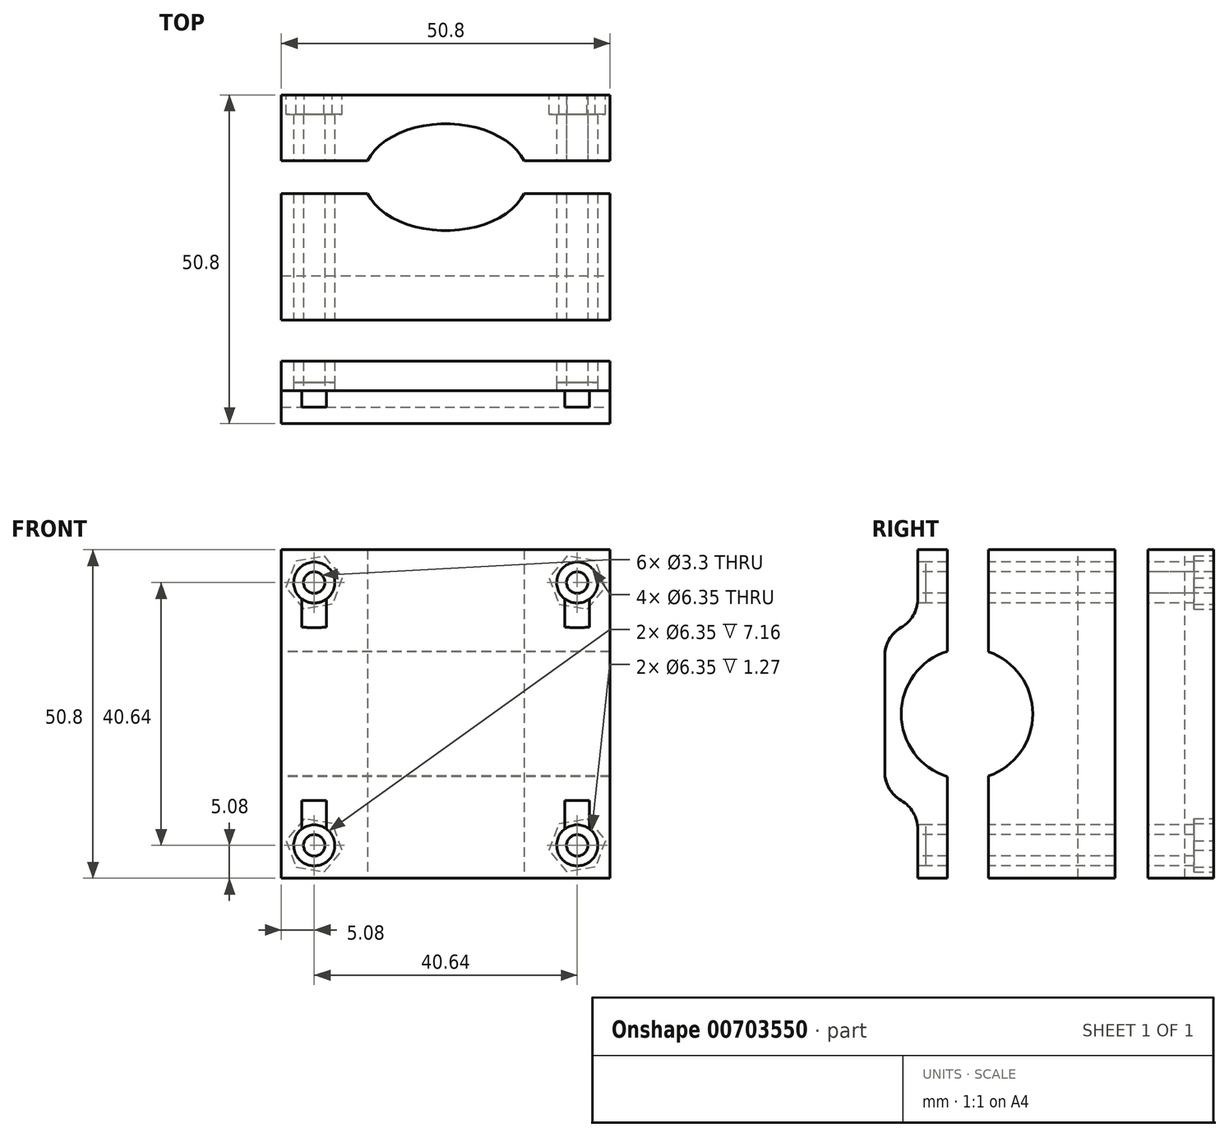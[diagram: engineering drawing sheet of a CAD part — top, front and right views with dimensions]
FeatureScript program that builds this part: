
annotation { "Feature Type Name" : "Feature", "Feature Type Description" : "" }
export const myFeature = defineFeature(function(context is Context, id is Id, definition is map)
    precondition{}
    {
        {
            var Q0;
            Q0=qCreatedBy(makeId("Top.planeOp"),FACE);
            var sketch = newSketch(context, id + "F0", { "sketchPlane" : qUnion([Q0])});
            skLineSegment(sketch, "E0.bottom", {"start": v(-25.4, -12.7) * mm, "end": v(25.4, -12.7) * mm});
            skLineSegment(sketch, "E0.top", {"start": v(-25.4, 12.7) * mm, "end": v(25.4, 12.7) * mm});
            skLineSegment(sketch, "E0.left", {"start": v(-25.4, -12.7) * mm, "end": v(-25.4, 12.7) * mm});
            skLineSegment(sketch, "E0.right", {"start": v(25.4, -12.7) * mm, "end": v(25.4, 12.7) * mm});
            skLineSegment(sketch, "E1.bottom", {"start": v(-25.4, 2.54) * mm, "end": v(25.4, 2.54) * mm});
            skLineSegment(sketch, "E1.top", {"start": v(-25.4, -2.54) * mm, "end": v(25.4, -2.54) * mm});
            skLineSegment(sketch, "E1.left", {"start": v(-25.4, 2.54) * mm, "end": v(-25.4, -2.54) * mm});
            skLineSegment(sketch, "E1.right", {"start": v(25.4, 2.54) * mm, "end": v(25.4, -2.54) * mm});
            skEllipse(sketch, "E2", {"center": v(0, 0) * mm, "majorRadius": 12.7 * mm, "minorRadius": 8.26 * mm, "majorAxis": v(1, 0)});
            skSolve(sketch);
        }
        {
            var Q0;
            {var subQ6=sQuery(id+"F0.wireOp",EDGE,"E0.top");Q0=makeQuery(id+"F0.imprint","IMPRINT",FACE,{"disambiguationData":[TD([[makeQuery(id+"F0.imprint","IMPRINT",EDGE,{"derivedFrom":subQ6}),-1.0]])]});}
            var Q1;
            {var subQ5=sQuery(id+"F0.wireOp",EDGE,"E0.bottom");Q1=makeQuery(id+"F0.imprint","IMPRINT",FACE,{"disambiguationData":[TD([[makeQuery(id+"F0.imprint","IMPRINT",EDGE,{"derivedFrom":subQ5}),1.0]])]});}
            extrude(context, id + "F1", {"entities" : qUnion([Q0, Q1]), "depth" : 25.4 * mm, "offsetDistance" : 25.4 * mm});
        }
        {
            var Q0;
            Q0=makeQuery(id+"F1.opExtrude","SWEPT_FACE",FACE,{"disambiguationData":[OSD([sQuery(id+"F0.wireOp",EDGE,"E0.bottom")])]});
            extrude(context, id + "F2", {"entities" : qUnion([Q0]), "operationType" : NewBodyOperationType.ADD, "depth" : 25.4 * mm, "offsetDistance" : 25.4 * mm});
        }
        {
            var Q0;
            {var subQ0=sQuery(id+"F0.wireOp",EDGE,"E0.right");var subQ1=sQuery(id+"F0.wireOp",EDGE,"E0.bottom");Q0=makeQuery(id+"F2.boolean.opBoolean","MERGE",FACE,{"derivedFrom":[makeQuery(id+"F1.opExtrude","SWEPT_FACE",FACE,{"disambiguationData":[OSD([subQ0]),TDD([makeQuery(id+"F0.imprint","IMPRINT",EDGE,{"disambiguationData":[TD([[makeQuery(id+"F0.imprint","INTERSECT",VERTEX,{"derivedFrom":[subQ1,subQ0]}),-1.0]])],"derivedFrom":subQ0})])]}),makeQuery(id+"F2.opExtrude","SWEPT_FACE",FACE,{"disambiguationData":[OSD([subQ1,subQ0])]})]});}
            var sketch = newSketch(context, id + "F3", { "sketchPlane" : qUnion([Q0])});
            skCircle(sketch, "E3", {"center": v(-25.4, 12.7) * mm, "radius": 10.16 * mm});
            skSolve(sketch);
        }
        {
            var Q0;
            Q0=makeQuery(id+"F3.imprint","IMPRINT",FACE,{"disambiguationData":[TD([[makeQuery(id+"F3.imprint","IMPRINT",EDGE,{"derivedFrom":sQuery(id+"F3.wireOp",EDGE,"E3")}),1.0]])]});
            extrude(context, id + "F4", {"entities" : qUnion([Q0]), "operationType" : NewBodyOperationType.REMOVE, "endBound" : BoundingType.THROUGH_ALL, "oppositeDirection" : true, "depth" : 25.4 * mm, "offsetDistance" : 25.4 * mm});
        }
        {
            var Q0;
            {var subQ0=sQuery(id+"F0.wireOp",EDGE,"E0.bottom");Q0=makeQuery(id+"F2.boolean.opBoolean","MERGE",FACE,{"derivedFrom":[makeQuery(id+"F1.opExtrude","CAP_FACE",FACE,{"disambiguationData":[OSD([subQ0,sQuery(id+"F0.wireOp",EDGE,"E0.left"),sQuery(id+"F0.wireOp",EDGE,"E0.right"),sQuery(id+"F0.wireOp",EDGE,"E1.top"),sQuery(id+"F0.wireOp",EDGE,"E2")])],"isStart":false}),makeQuery(id+"F2.opExtrude","SWEPT_FACE",FACE,{"disambiguationData":[OSD([subQ0]),TDD([makeQuery(id+"F1.opExtrude","CAP_EDGE",EDGE,{"disambiguationData":[OSD([subQ0])],"isStart":false})])]})]});}
            var Q1;
            Q1=makeQuery(id+"F1.opExtrude","CAP_FACE",FACE,{"disambiguationData":[OSD([sQuery(id+"F0.wireOp",EDGE,"E0.top"),sQuery(id+"F0.wireOp",EDGE,"E0.left"),sQuery(id+"F0.wireOp",EDGE,"E0.right"),sQuery(id+"F0.wireOp",EDGE,"E1.bottom"),sQuery(id+"F0.wireOp",EDGE,"E2")])],"isStart":false});
            extrude(context, id + "F5", {"entities" : qUnion([Q0, Q1]), "operationType" : NewBodyOperationType.ADD, "depth" : 12.7 * mm, "offsetDistance" : 25.4 * mm});
        }
        {
            var Q0;
            {var subQ0=sQuery(id+"F0.wireOp",EDGE,"E0.bottom");Q0=makeQuery(id+"F2.boolean.opBoolean","MERGE",FACE,{"derivedFrom":[makeQuery(id+"F1.opExtrude","CAP_FACE",FACE,{"disambiguationData":[OSD([subQ0,sQuery(id+"F0.wireOp",EDGE,"E0.left"),sQuery(id+"F0.wireOp",EDGE,"E0.right"),sQuery(id+"F0.wireOp",EDGE,"E1.top"),sQuery(id+"F0.wireOp",EDGE,"E2")])],"isStart":true}),makeQuery(id+"F2.opExtrude","SWEPT_FACE",FACE,{"disambiguationData":[OSD([subQ0]),TDD([makeQuery(id+"F1.opExtrude","CAP_EDGE",EDGE,{"disambiguationData":[OSD([subQ0])],"isStart":true})])]})]});}
            var Q1;
            Q1=makeQuery(id+"F1.opExtrude","CAP_FACE",FACE,{"disambiguationData":[OSD([sQuery(id+"F0.wireOp",EDGE,"E0.top"),sQuery(id+"F0.wireOp",EDGE,"E0.left"),sQuery(id+"F0.wireOp",EDGE,"E0.right"),sQuery(id+"F0.wireOp",EDGE,"E1.bottom"),sQuery(id+"F0.wireOp",EDGE,"E2")])],"isStart":true});
            extrude(context, id + "F6", {"entities" : qUnion([Q0, Q1]), "operationType" : NewBodyOperationType.ADD, "depth" : 12.7 * mm, "offsetDistance" : 25.4 * mm});
        }
        {
            var Q0;
            {var subQ0=sQuery(id+"F0.wireOp",EDGE,"E0.bottom");Q0=makeQuery(id+"F6.boolean.opBoolean","MERGE",FACE,{"derivedFrom":[makeQuery(id+"F5.boolean.opBoolean","MERGE",FACE,{"derivedFrom":[makeQuery(id+"F2.opExtrude","CAP_FACE",FACE,{"disambiguationData":[OSD([subQ0])],"isStart":false}),makeQuery(id+"F5.opExtrude","SWEPT_FACE",FACE,{"disambiguationData":[OSD([subQ0])]})]}),makeQuery(id+"F6.opExtrude","SWEPT_FACE",FACE,{"disambiguationData":[OSD([subQ0])]})]});}
            var sketch = newSketch(context, id + "F7", { "sketchPlane" : qUnion([Q0])});
            skLineSegment(sketch, "E4.bottom", {"start": v(-25.4, 38.1) * mm, "end": v(25.4, 38.1) * mm});
            skLineSegment(sketch, "E4.top", {"start": v(-25.4, 25.4) * mm, "end": v(25.4, 25.4) * mm});
            skLineSegment(sketch, "E4.left", {"start": v(-25.4, 38.1) * mm, "end": v(-25.4, 25.4) * mm});
            skLineSegment(sketch, "E4.right", {"start": v(25.4, 38.1) * mm, "end": v(25.4, 25.4) * mm});
            skLineSegment(sketch, "E5", {"start": v(-25.4, 12.7) * mm, "end": v(25.4, 12.7) * mm});
            skLineSegment(sketch, "E6.MirrorCS", {"start": v(-25.4, 0) * mm, "end": v(25.4, 0) * mm});
            skSolve(sketch);
        }
        {
            var Q0;
            {var subQ0=sQuery(id+"F7.wireOp",EDGE,"E6.MirrorCS");Q0=makeQuery(id+"F7.imprint","IMPRINT",FACE,{"disambiguationData":[TD([[makeQuery(id+"F7.imprint","IMPRINT",EDGE,{"derivedFrom":subQ0}),-1.0]])]});}
            var Q1;
            Q1=makeQuery(id+"F7.imprint","IMPRINT",FACE,{"disambiguationData":[TD([[makeQuery(id+"F7.imprint","IMPRINT",EDGE,{"derivedFrom":sQuery(id+"F7.wireOp",EDGE,"E4.bottom")}),-1.0]])]});
            extrude(context, id + "F8", {"entities" : qUnion([Q0, Q1]), "operationType" : NewBodyOperationType.REMOVE, "oppositeDirection" : true, "depth" : 5.08 * mm, "offsetDistance" : 25.4 * mm});
        }
        {
            var Q0;
            {var subQ0=sQuery(id+"F0.wireOp",EDGE,"E0.bottom");Q0=makeQuery(id+"F6.boolean.opBoolean","MERGE",FACE,{"derivedFrom":[makeQuery(id+"F5.boolean.opBoolean","MERGE",FACE,{"derivedFrom":[makeQuery(id+"F2.opExtrude","CAP_FACE",FACE,{"disambiguationData":[OSD([subQ0])],"isStart":false}),makeQuery(id+"F5.opExtrude","SWEPT_FACE",FACE,{"disambiguationData":[OSD([subQ0])]})]}),makeQuery(id+"F6.opExtrude","SWEPT_FACE",FACE,{"disambiguationData":[OSD([subQ0])]})]});}
            var sketch = newSketch(context, id + "F9", { "sketchPlane" : qUnion([Q0])});
            skLineSegment(sketch, "E7", {"start": v(-25.4, 12.7) * mm, "end": v(25.4, 12.7) * mm});
            skCircle(sketch, "E8", {"center": v(-20.32, 33.02) * mm, "radius": 3.18 * mm});
            skCircle(sketch, "E9.MirrorC", {"center": v(20.32, 33.02) * mm, "radius": 3.18 * mm});
            skCircle(sketch, "E10.MirrorC", {"center": v(-20.32, -7.62) * mm, "radius": 3.18 * mm});
            skCircle(sketch, "E11.MirrorC", {"center": v(20.32, -7.62) * mm, "radius": 3.18 * mm});
            skCircle(sketch, "E12", {"center": v(-20.32, 33.02) * mm, "radius": 1.65 * mm});
            skCircle(sketch, "E13.MirrorC", {"center": v(20.32, 33.02) * mm, "radius": 1.65 * mm});
            skCircle(sketch, "E14.MirrorC", {"center": v(-20.32, -7.62) * mm, "radius": 1.65 * mm});
            skCircle(sketch, "E15.MirrorC", {"center": v(20.32, -7.62) * mm, "radius": 1.65 * mm});
            skSolve(sketch);
        }
        {
            var Q0;
            Q0=makeQuery(id+"F9.imprint","IMPRINT",FACE,{"disambiguationData":[TD([[makeQuery(id+"F9.imprint","IMPRINT",EDGE,{"derivedFrom":sQuery(id+"F9.wireOp",EDGE,"E12")}),1.0]])]});
            var Q1;
            Q1=makeQuery(id+"F9.imprint","IMPRINT",FACE,{"disambiguationData":[TD([[makeQuery(id+"F9.imprint","IMPRINT",EDGE,{"derivedFrom":sQuery(id+"F9.wireOp",EDGE,"E13.MirrorC")}),-1.0]])]});
            var Q2;
            Q2=makeQuery(id+"F9.imprint","IMPRINT",FACE,{"disambiguationData":[TD([[makeQuery(id+"F9.imprint","IMPRINT",EDGE,{"derivedFrom":sQuery(id+"F9.wireOp",EDGE,"E15.MirrorC")}),1.0]])]});
            var Q3;
            Q3=makeQuery(id+"F9.imprint","IMPRINT",FACE,{"disambiguationData":[TD([[makeQuery(id+"F9.imprint","IMPRINT",EDGE,{"derivedFrom":sQuery(id+"F9.wireOp",EDGE,"E14.MirrorC")}),-1.0]])]});
            extrude(context, id + "F10", {"entities" : qUnion([Q0, Q1, Q2, Q3]), "operationType" : NewBodyOperationType.REMOVE, "endBound" : BoundingType.THROUGH_ALL, "oppositeDirection" : true, "depth" : 25.4 * mm, "offsetDistance" : 25.4 * mm});
        }
        {
            var Q0;
            Q0=makeQuery(id+"F9.imprint","IMPRINT",FACE,{"disambiguationData":[TD([[makeQuery(id+"F9.imprint","IMPRINT",EDGE,{"derivedFrom":sQuery(id+"F9.wireOp",EDGE,"E8")}),1.0]])]});
            var Q1;
            Q1=makeQuery(id+"F9.imprint","IMPRINT",FACE,{"disambiguationData":[TD([[makeQuery(id+"F9.imprint","IMPRINT",EDGE,{"derivedFrom":sQuery(id+"F9.wireOp",EDGE,"E10.MirrorC")}),-1.0]])]});
            var Q2;
            Q2=makeQuery(id+"F9.imprint","IMPRINT",FACE,{"disambiguationData":[TD([[makeQuery(id+"F9.imprint","IMPRINT",EDGE,{"derivedFrom":sQuery(id+"F9.wireOp",EDGE,"E11.MirrorC")}),1.0]])]});
            var Q3;
            Q3=makeQuery(id+"F9.imprint","IMPRINT",FACE,{"disambiguationData":[TD([[makeQuery(id+"F9.imprint","IMPRINT",EDGE,{"derivedFrom":sQuery(id+"F9.wireOp",EDGE,"E9.MirrorC")}),-1.0]])]});
            extrude(context, id + "F11", {"entities" : qUnion([Q0, Q1, Q2, Q3]), "operationType" : NewBodyOperationType.REMOVE, "oppositeDirection" : true, "depth" : 6.35 * mm, "offsetDistance" : 25.4 * mm});
        }
        {
            var Q0;
            {var subQ0=sQuery(id+"F0.wireOp",EDGE,"E0.left");var subQ1=sQuery(id+"F0.wireOp",EDGE,"E0.bottom");Q0=makeQuery(id+"F6.boolean.opBoolean","MERGE",FACE,{"derivedFrom":[makeQuery(id+"F5.boolean.opBoolean","MERGE",FACE,{"derivedFrom":[makeQuery(id+"F2.boolean.opBoolean","MERGE",FACE,{"derivedFrom":[makeQuery(id+"F1.opExtrude","SWEPT_FACE",FACE,{"disambiguationData":[OSD([subQ0]),TDD([makeQuery(id+"F0.imprint","IMPRINT",EDGE,{"disambiguationData":[TD([[makeQuery(id+"F0.imprint","INTERSECT",VERTEX,{"derivedFrom":[subQ1,subQ0]}),-1.0]])],"derivedFrom":subQ0})])]}),makeQuery(id+"F2.opExtrude","SWEPT_FACE",FACE,{"disambiguationData":[OSD([subQ1,subQ0])]})]}),makeQuery(id+"F5.opExtrude","SWEPT_FACE",FACE,{"disambiguationData":[OSD([subQ1,subQ0])]})]}),makeQuery(id+"F6.opExtrude","SWEPT_FACE",FACE,{"disambiguationData":[OSD([subQ1,subQ0])]})]});}
            var sketch = newSketch(context, id + "F12", { "sketchPlane" : qUnion([Q0])});
            skLineSegment(sketch, "E16.bottom", {"start": v(22.1, 38.1) * mm, "end": v(28.45, 38.1) * mm});
            skLineSegment(sketch, "E16.top", {"start": v(22.1, -12.7) * mm, "end": v(28.45, -12.7) * mm});
            skLineSegment(sketch, "E16.left", {"start": v(22.1, 38.1) * mm, "end": v(22.1, -12.7) * mm});
            skLineSegment(sketch, "E16.right", {"start": v(28.45, 38.1) * mm, "end": v(28.45, -12.7) * mm});
            skSolve(sketch);
        }
        {
            var Q0;
            {var subQ0=sQuery(id+"F12.wireOp",EDGE,"E16.bottom");Q0=makeQuery(id+"F12.imprint","IMPRINT",FACE,{"disambiguationData":[TD([[makeQuery(id+"F12.imprint","IMPRINT",EDGE,{"derivedFrom":subQ0}),1.0]])]});}
            var Q1;
            {var subQ0=sQuery(id+"F12.wireOp",EDGE,"E16.top");Q1=makeQuery(id+"F12.imprint","IMPRINT",FACE,{"disambiguationData":[TD([[makeQuery(id+"F12.imprint","IMPRINT",EDGE,{"derivedFrom":subQ0}),-1.0]])]});}
            extrude(context, id + "F13", {"entities" : qUnion([Q0, Q1]), "operationType" : NewBodyOperationType.REMOVE, "endBound" : BoundingType.THROUGH_ALL, "oppositeDirection" : true, "depth" : 25.4 * mm, "offsetDistance" : 25.4 * mm});
        }
        {
            var Q0;
            {var subQ0=sQuery(id+"F0.wireOp",EDGE,"E0.top");Q0=makeQuery(id+"F6.boolean.opBoolean","MERGE",FACE,{"derivedFrom":[makeQuery(id+"F5.boolean.opBoolean","MERGE",FACE,{"derivedFrom":[makeQuery(id+"F1.opExtrude","SWEPT_FACE",FACE,{"disambiguationData":[OSD([subQ0])]}),makeQuery(id+"F5.opExtrude","SWEPT_FACE",FACE,{"disambiguationData":[OSD([subQ0])]})]}),makeQuery(id+"F6.opExtrude","SWEPT_FACE",FACE,{"disambiguationData":[OSD([subQ0])]})]});}
            var sketch = newSketch(context, id + "F14", { "sketchPlane" : qUnion([Q0])});
            skCircle(sketch, "E17.cCircle", {"center": v(-20.32, 33.02) * mm, "radius": 4.39 * mm, "construction": true});
            skLineSegment(sketch, "E17.0", {"start": v(-16, 33.75) * mm, "end": v(-17.52, 29.64) * mm});
            skLineSegment(sketch, "E17.1", {"start": v(-17.52, 29.64) * mm, "end": v(-21.85, 28.9) * mm});
            skLineSegment(sketch, "E17.2", {"start": v(-21.85, 28.9) * mm, "end": v(-24.65, 32.29) * mm});
            skLineSegment(sketch, "E17.3", {"start": v(-24.65, 32.29) * mm, "end": v(-23.12, 36.4) * mm});
            skLineSegment(sketch, "E17.4", {"start": v(-23.12, 36.4) * mm, "end": v(-18.8, 37.13) * mm});
            skLineSegment(sketch, "E17.5", {"start": v(-18.8, 37.13) * mm, "end": v(-16, 33.75) * mm});
            skLineSegment(sketch, "E18.MirrorCS", {"start": v(21.85, 28.9) * mm, "end": v(24.65, 32.29) * mm});
            skLineSegment(sketch, "E19.MirrorCS", {"start": v(24.65, 32.29) * mm, "end": v(23.12, 36.4) * mm});
            skLineSegment(sketch, "E20.MirrorCS", {"start": v(17.52, 29.64) * mm, "end": v(21.85, 28.9) * mm});
            skLineSegment(sketch, "E21.MirrorCS", {"start": v(16, 33.75) * mm, "end": v(17.52, 29.64) * mm});
            skLineSegment(sketch, "E22.MirrorCS", {"start": v(23.12, 36.4) * mm, "end": v(18.8, 37.13) * mm});
            skLineSegment(sketch, "E23.MirrorCS", {"start": v(18.8, 37.13) * mm, "end": v(16, 33.75) * mm});
            skLineSegment(sketch, "E24.MirrorCS", {"start": v(-17.52, -4.24) * mm, "end": v(-21.85, -3.5) * mm});
            skLineSegment(sketch, "E25.MirrorCS", {"start": v(-16, -8.35) * mm, "end": v(-17.52, -4.24) * mm});
            skLineSegment(sketch, "E26.MirrorCS", {"start": v(-21.85, -3.5) * mm, "end": v(-24.65, -6.89) * mm});
            skLineSegment(sketch, "E27.MirrorCS", {"start": v(-24.65, -6.89) * mm, "end": v(-23.12, -11) * mm});
            skLineSegment(sketch, "E28.MirrorCS", {"start": v(-23.12, -11) * mm, "end": v(-18.8, -11.73) * mm});
            skLineSegment(sketch, "E29.MirrorCS", {"start": v(-18.8, -11.73) * mm, "end": v(-16, -8.35) * mm});
            skLineSegment(sketch, "E30.MirrorCS", {"start": v(17.52, -4.24) * mm, "end": v(21.85, -3.5) * mm});
            skLineSegment(sketch, "E31.MirrorCS", {"start": v(21.85, -3.5) * mm, "end": v(24.65, -6.89) * mm});
            skLineSegment(sketch, "E32.MirrorCS", {"start": v(24.65, -6.89) * mm, "end": v(23.12, -11) * mm});
            skLineSegment(sketch, "E33.MirrorCS", {"start": v(23.12, -11) * mm, "end": v(18.8, -11.73) * mm});
            skLineSegment(sketch, "E34.MirrorCS", {"start": v(18.8, -11.73) * mm, "end": v(16, -8.35) * mm});
            skLineSegment(sketch, "E35.MirrorCS", {"start": v(16, -8.35) * mm, "end": v(17.52, -4.24) * mm});
            skSolve(sketch);
        }
        {
            var Q0;
            Q0=makeQuery(id+"F14.imprint","IMPRINT",FACE,{"disambiguationData":[TD([[makeQuery(id+"F14.imprint","IMPRINT",EDGE,{"derivedFrom":sQuery(id+"F14.wireOp",EDGE,"E17.0")}),-1.0]])]});
            var Q1;
            Q1=makeQuery(id+"F14.imprint","IMPRINT",FACE,{"disambiguationData":[TD([[makeQuery(id+"F14.imprint","IMPRINT",EDGE,{"derivedFrom":sQuery(id+"F14.wireOp",EDGE,"E18.MirrorCS")}),1.0]])]});
            var Q2;
            Q2=makeQuery(id+"F14.imprint","IMPRINT",FACE,{"disambiguationData":[TD([[makeQuery(id+"F14.imprint","IMPRINT",EDGE,{"derivedFrom":sQuery(id+"F14.wireOp",EDGE,"E30.MirrorCS")}),-1.0]])]});
            var Q3;
            Q3=makeQuery(id+"F14.imprint","IMPRINT",FACE,{"disambiguationData":[TD([[makeQuery(id+"F14.imprint","IMPRINT",EDGE,{"derivedFrom":sQuery(id+"F14.wireOp",EDGE,"E24.MirrorCS")}),1.0]])]});
            extrude(context, id + "F15", {"entities" : qUnion([Q0, Q1, Q2, Q3]), "operationType" : NewBodyOperationType.REMOVE, "oppositeDirection" : true, "depth" : 3 * mm, "offsetDistance" : 25.4 * mm, "hasSecondDirectionOffset" : true, "secondDirectionOffsetDistance" : 2.54 * mm});
        }
        {
            var Q0;
            Q0=makeQuery(id+"F8.boolean.opBoolean","COPY",EDGE,{"derivedFrom":makeQuery(id+"F8.opExtrude","CAP_EDGE",EDGE,{"disambiguationData":[OSD([sQuery(id+"F7.wireOp",EDGE,"E6.MirrorCS")])],"isStart":false})});
            var Q1;
            Q1=makeQuery(id+"F8.boolean.opBoolean","COPY",EDGE,{"derivedFrom":makeQuery(id+"F8.opExtrude","CAP_EDGE",EDGE,{"disambiguationData":[OSD([sQuery(id+"F7.wireOp",EDGE,"E4.top")])],"isStart":false})});
            fillet(context, id + "F16", {"entities" : qUnion([Q0, Q1]), "tangentPropagation" : true, "radius" : 5.08 * mm, "defaultsChanged" : false, "vertexSettings" : [], "allowEdgeOverflow" : false});
        }
        {
            var Q0;
            {var subQ0=sQuery(id+"F0.wireOp",EDGE,"E0.bottom");Q0=makeQuery(id+"F16.opFillet","BLEND_EDGE",EDGE,{"disambiguationData":[OD(2.0)],"blendedFrom":[makeQuery(id+"F8.boolean.opBoolean","COPY",EDGE,{"derivedFrom":makeQuery(id+"F8.opExtrude","CAP_EDGE",EDGE,{"disambiguationData":[OSD([sQuery(id+"F7.wireOp",EDGE,"E4.top")])],"isStart":false})}),makeQuery(id+"F6.boolean.opBoolean","MERGE",FACE,{"derivedFrom":[makeQuery(id+"F5.boolean.opBoolean","MERGE",FACE,{"derivedFrom":[makeQuery(id+"F2.opExtrude","CAP_FACE",FACE,{"disambiguationData":[OSD([subQ0])],"isStart":false}),makeQuery(id+"F5.opExtrude","SWEPT_FACE",FACE,{"disambiguationData":[OSD([subQ0])]})]}),makeQuery(id+"F6.opExtrude","SWEPT_FACE",FACE,{"disambiguationData":[OSD([subQ0])]})]})],"blendedInto":[makeQuery(id+"F6.boolean.opBoolean","MERGE",FACE,{"derivedFrom":[makeQuery(id+"F5.boolean.opBoolean","MERGE",FACE,{"derivedFrom":[makeQuery(id+"F2.opExtrude","CAP_FACE",FACE,{"disambiguationData":[OSD([subQ0])],"isStart":false}),makeQuery(id+"F5.opExtrude","SWEPT_FACE",FACE,{"disambiguationData":[OSD([subQ0])]})]}),makeQuery(id+"F6.opExtrude","SWEPT_FACE",FACE,{"disambiguationData":[OSD([subQ0])]})]})]});}
            var Q1;
            {var subQ0=sQuery(id+"F0.wireOp",EDGE,"E0.bottom");Q1=makeQuery(id+"F16.opFillet","BLEND_EDGE",EDGE,{"disambiguationData":[OD(2.0)],"blendedFrom":[makeQuery(id+"F8.boolean.opBoolean","COPY",EDGE,{"derivedFrom":makeQuery(id+"F8.opExtrude","CAP_EDGE",EDGE,{"disambiguationData":[OSD([sQuery(id+"F7.wireOp",EDGE,"E6.MirrorCS")])],"isStart":false})}),makeQuery(id+"F6.boolean.opBoolean","MERGE",FACE,{"derivedFrom":[makeQuery(id+"F5.boolean.opBoolean","MERGE",FACE,{"derivedFrom":[makeQuery(id+"F2.opExtrude","CAP_FACE",FACE,{"disambiguationData":[OSD([subQ0])],"isStart":false}),makeQuery(id+"F5.opExtrude","SWEPT_FACE",FACE,{"disambiguationData":[OSD([subQ0])]})]}),makeQuery(id+"F6.opExtrude","SWEPT_FACE",FACE,{"disambiguationData":[OSD([subQ0])]})]})],"blendedInto":[makeQuery(id+"F6.boolean.opBoolean","MERGE",FACE,{"derivedFrom":[makeQuery(id+"F5.boolean.opBoolean","MERGE",FACE,{"derivedFrom":[makeQuery(id+"F2.opExtrude","CAP_FACE",FACE,{"disambiguationData":[OSD([subQ0])],"isStart":false}),makeQuery(id+"F5.opExtrude","SWEPT_FACE",FACE,{"disambiguationData":[OSD([subQ0])]})]}),makeQuery(id+"F6.opExtrude","SWEPT_FACE",FACE,{"disambiguationData":[OSD([subQ0])]})]})]});}
            fillet(context, id + "F17", {"entities" : qUnion([Q0, Q1]), "tangentPropagation" : true, "radius" : 5.08 * mm, "defaultsChanged" : false, "vertexSettings" : [], "allowEdgeOverflow" : false});
        }
    });
